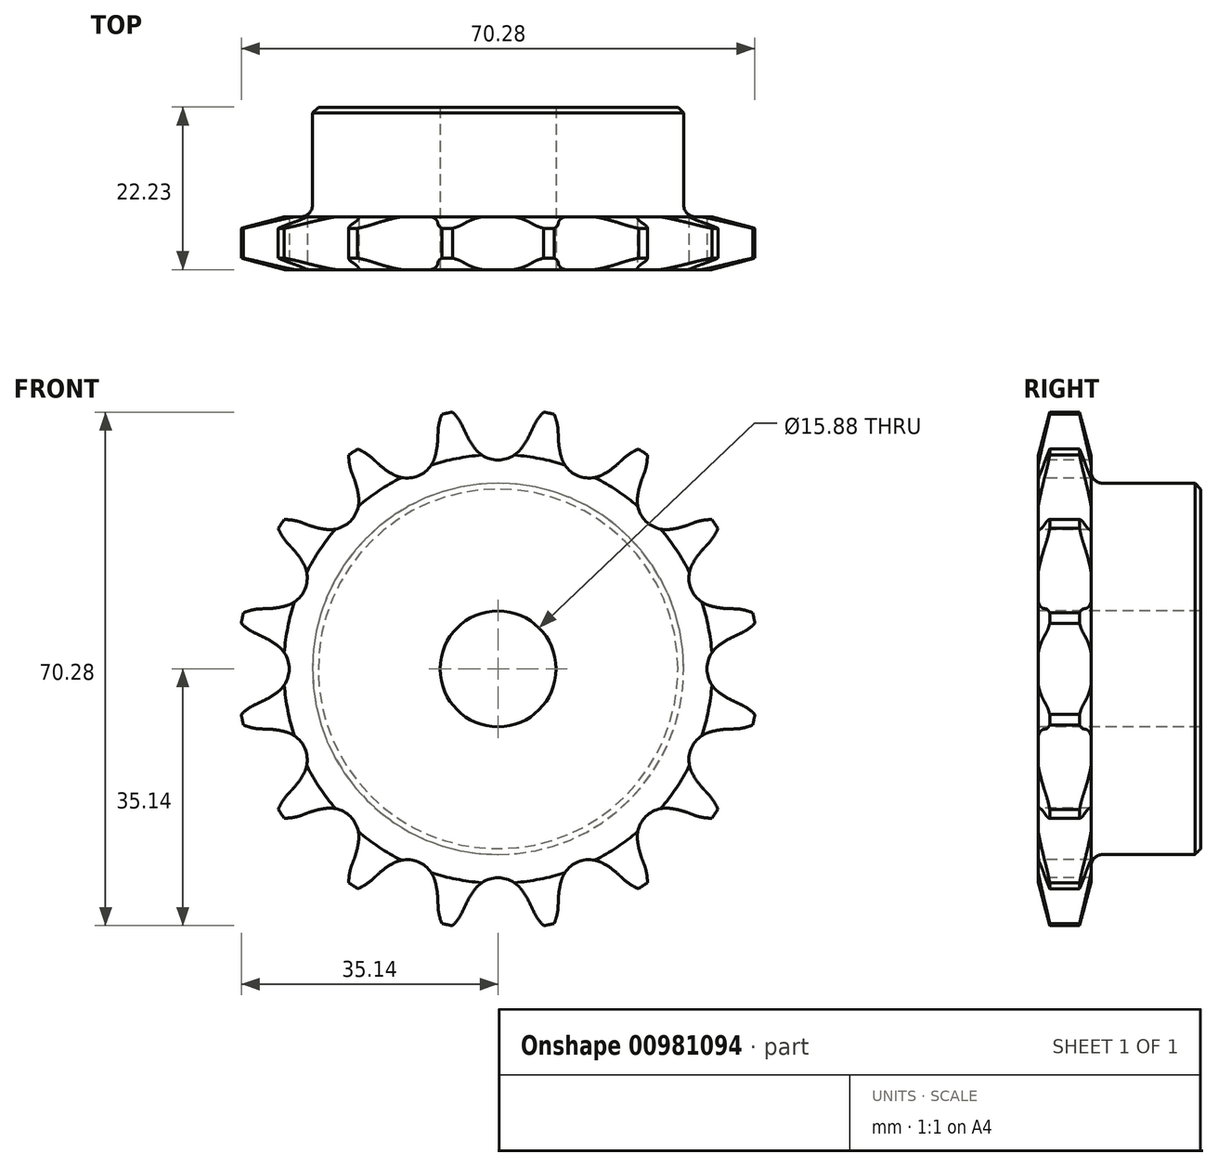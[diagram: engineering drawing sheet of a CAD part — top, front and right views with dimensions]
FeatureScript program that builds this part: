
annotation { "Feature Type Name" : "Feature", "Feature Type Description" : "" }
export const myFeature = defineFeature(function(context is Context, id is Id, definition is map)
    precondition{}
    {
        {
            var Q0;
            Q0=qCreatedBy(makeId("Right.planeOp"),FACE);
            var sketch = newSketch(context, id + "F0", { "sketchPlane" : qUnion([Q0])});
            skLineSegment(sketch, "E0", {"start": v(0, 0) * mm, "end": v(22.23, 0) * mm, "construction": true});
            skLineSegment(sketch, "E1.bottom", {"start": v(0, 35.69) * mm, "end": v(7.21, 35.69) * mm});
            skLineSegment(sketch, "E1.top", {"start": v(0, 7.94) * mm, "end": v(7.21, 7.94) * mm});
            skLineSegment(sketch, "E1.left", {"start": v(0, 35.69) * mm, "end": v(0, 7.94) * mm});
            skLineSegment(sketch, "E1.right", {"start": v(7.21, 35.69) * mm, "end": v(7.21, 7.94) * mm});
            skLineSegment(sketch, "E2.bottom", {"start": v(0, 7.94) * mm, "end": v(22.23, 7.94) * mm});
            skLineSegment(sketch, "E2.top", {"start": v(0, 25.4) * mm, "end": v(22.23, 25.4) * mm});
            skLineSegment(sketch, "E2.left", {"start": v(0, 7.94) * mm, "end": v(0, 25.4) * mm});
            skLineSegment(sketch, "E2.right", {"start": v(22.23, 7.94) * mm, "end": v(22.23, 25.4) * mm});
            skLineSegment(sketch, "E3.MirrorCS", {"start": v(0, -7.94) * mm, "end": v(7.21, -7.94) * mm});
            skLineSegment(sketch, "E4.MirrorCS", {"start": v(22.23, -7.94) * mm, "end": v(22.23, -25.4) * mm});
            skLineSegment(sketch, "E5.MirrorCS", {"start": v(0, -7.94) * mm, "end": v(22.23, -7.94) * mm});
            skLineSegment(sketch, "E6.MirrorCS", {"start": v(0, -35.69) * mm, "end": v(7.21, -35.69) * mm});
            skLineSegment(sketch, "E7.MirrorCS", {"start": v(0, -7.94) * mm, "end": v(0, -25.4) * mm});
            skLineSegment(sketch, "E8.MirrorCS", {"start": v(0, -25.4) * mm, "end": v(22.23, -25.4) * mm});
            skLineSegment(sketch, "E9.MirrorCS", {"start": v(0, -35.69) * mm, "end": v(0, -7.94) * mm});
            skLineSegment(sketch, "E10.MirrorCS", {"start": v(7.21, -35.69) * mm, "end": v(7.21, -7.94) * mm});
            skSolve(sketch);
        }
        {
            var Q0;
            {var subQ0=sQuery(id+"F0.wireOp",EDGE,"E1.bottom");Q0=makeQuery(id+"F0.imprint","IMPRINT",FACE,{"disambiguationData":[TD([[makeQuery(id+"F0.imprint","IMPRINT",EDGE,{"derivedFrom":subQ0}),-1.0]])]});}
            var Q1;
            {var subQ0=sQuery(id+"F0.wireOp",EDGE,"E1.top");Q1=makeQuery(id+"F0.imprint","IMPRINT",FACE,{"disambiguationData":[TD([[makeQuery(id+"F0.imprint","IMPRINT",EDGE,{"derivedFrom":subQ0}),1.0]])]});}
            var Q2;
            {var subQ0=sQuery(id+"F0.wireOp",EDGE,"E2.bottom");Q2=makeQuery(id+"F0.imprint","IMPRINT",FACE,{"disambiguationData":[TD([[makeQuery(id+"F0.imprint","IMPRINT",EDGE,{"derivedFrom":subQ0}),1.0]])]});}
            var Q3;
            Q3=sQuery(id+"F0.wireOp",EDGE,"E0");
            revolve(context, id + "F1", {"surfaceOperationType" : NewSurfaceOperationType.NEW, "entities" : qUnion([Q0, Q1, Q2]), "axis" : qUnion([Q3]), "revolveType" : RevolveType.FULL});
        }
        {
            var Q0;
            Q0=makeQuery(id+"F1.opRevolve","SWEPT_EDGE",EDGE,{"disambiguationData":[OSD([sQuery(id+"F0.wireOp",EDGE,"E1.right"),sQuery(id+"F0.wireOp",EDGE,"E2.top")])]});
            fillet(context, id + "F2", {"entities" : qUnion([Q0]), "radius" : 1.59 * mm, "tangentPropagation" : true, "allowEdgeOverflow" : false});
        }
        {
            var Q0;
            Q0=makeQuery(id+"F1.opRevolve","SWEPT_EDGE",EDGE,{"disambiguationData":[OSD([sQuery(id+"F0.wireOp",EDGE,"E2.top"),sQuery(id+"F0.wireOp",EDGE,"E2.right")])]});
            chamfer(context, id + "F3", {"entities" : qUnion([Q0]), "width" : 0.8 * mm, "tangentPropagation" : true});
        }
        {
            var Q0;
            Q0=makeQuery(id+"F1.opRevolve","SWEPT_EDGE",EDGE,{"disambiguationData":[OSD([sQuery(id+"F0.wireOp",EDGE,"E1.bottom"),sQuery(id+"F0.wireOp",EDGE,"E1.left")])]});
            var Q1;
            Q1=makeQuery(id+"F1.opRevolve","SWEPT_EDGE",EDGE,{"disambiguationData":[OSD([sQuery(id+"F0.wireOp",EDGE,"E1.bottom"),sQuery(id+"F0.wireOp",EDGE,"E1.right")])]});
            chamfer(context, id + "F4", {"entities" : qUnion([Q0, Q1]), "chamferType" : ChamferType.TWO_OFFSETS, "width1" : 6.35 * mm, "oppositeDirection" : false, "width2" : 1.57 * mm, "tangentPropagation" : true});
        }
        {
            var Q0;
            Q0=makeQuery(id+"F1.opRevolve","SWEPT_FACE",FACE,{"disambiguationData":[OSD([sQuery(id+"F0.wireOp",EDGE,"E1.left")])]});
            var sketch = newSketch(context, id + "F5", { "sketchPlane" : qUnion([Q0])});
            skCircle(sketch, "E11", {"center": v(0, 0) * mm, "radius": 32.55 * mm, "construction": true});
            skLineSegment(sketch, "E12", {"start": v(0, 0) * mm, "end": v(0, 32.55) * mm, "construction": true});
            skLineSegment(sketch, "E13", {"start": v(0, 32.55) * mm, "end": v(48.47, 32.55) * mm, "construction": true});
            skLineSegment(sketch, "E14", {"start": v(0, 32.55) * mm, "end": v(5, 36.56) * mm, "construction": true});
            skLineSegment(sketch, "E15", {"start": v(5, 36.56) * mm, "end": v(-4.46, 32.3) * mm, "construction": true});
            skLineSegment(sketch, "E16", {"start": v(-4.46, 32.3) * mm, "end": v(-4.82, 33.1) * mm});
            skLineSegment(sketch, "E17", {"start": v(0, 0) * mm, "end": v(-7.13, 35.85) * mm, "construction": true});
            skArc(sketch, "E18", {"start": v(-7.13, 35.85) * mm, "mid": v(-15.87, 26.15) * mm, "end": v(-4.82, 33.1) * mm, "construction": true});
            skArc(sketch, "E19", {"start": v(-4.82, 33.1) * mm, "mid": v(-5.78, 34.63) * mm, "end": v(-7.13, 35.85) * mm});
            skLineSegment(sketch, "E20", {"start": v(-4.46, 32.3) * mm, "end": v(-4.46, 32.3) * mm});
            skLineSegment(sketch, "E21", {"start": v(-4.82, 33.1) * mm, "end": v(-8.15, 40.5) * mm, "construction": true});
            skArc(sketch, "E22", {"start": v(-4.46, 32.3) * mm, "mid": v(-3.84, 31.14) * mm, "end": v(-3.1, 30.07) * mm});
            skLineSegment(sketch, "E23", {"start": v(-3.1, 30.07) * mm, "end": v(-3.1, 30.07) * mm});
            skArc(sketch, "E24.MirrorCS", {"start": v(4.46, 32.3) * mm, "mid": v(3.84, 31.14) * mm, "end": v(3.1, 30.07) * mm});
            skLineSegment(sketch, "E25.MirrorCS", {"start": v(4.46, 32.3) * mm, "end": v(4.82, 33.1) * mm});
            skArc(sketch, "E26.MirrorCS", {"start": v(4.82, 33.1) * mm, "mid": v(5.78, 34.63) * mm, "end": v(7.13, 35.85) * mm});
            skArc(sketch, "E27", {"start": v(-3.1, 30.07) * mm, "mid": v(13.83, 41.97) * mm, "end": v(-4.46, 32.3) * mm, "construction": true});
            skArc(sketch, "E28", {"start": v(3.1, 30.07) * mm, "mid": v(0, 36.51) * mm, "end": v(-3.1, 30.07) * mm, "construction": true});
            skArc(sketch, "E29", {"start": v(-3.1, 30.07) * mm, "mid": v(0, 28.59) * mm, "end": v(3.1, 30.07) * mm});
            skArc(sketch, "E30.1.0", {"start": v(-17.12, 28.74) * mm, "mid": v(-18.6, 29.79) * mm, "end": v(-20.3, 30.4) * mm});
            skLineSegment(sketch, "E30.1.1", {"start": v(-16.48, 28.14) * mm, "end": v(-17.12, 28.74) * mm});
            skArc(sketch, "E30.1.2", {"start": v(-16.48, 28.14) * mm, "mid": v(-15.47, 27.3) * mm, "end": v(-14.36, 26.6) * mm});
            skArc(sketch, "E30.1.3", {"start": v(-14.36, 26.6) * mm, "mid": v(-10.94, 26.41) * mm, "end": v(-8.65, 28.96) * mm});
            skArc(sketch, "E30.1.4", {"start": v(-8.24, 31.55) * mm, "mid": v(-8.37, 30.24) * mm, "end": v(-8.65, 28.96) * mm});
            skLineSegment(sketch, "E30.1.5", {"start": v(-8.24, 31.55) * mm, "end": v(-8.22, 32.42) * mm});
            skArc(sketch, "E30.1.6", {"start": v(-8.22, 32.42) * mm, "mid": v(-7.91, 34.21) * mm, "end": v(-7.13, 35.85) * mm});
            skArc(sketch, "E30.2.0", {"start": v(-26.8, 20) * mm, "mid": v(-28.58, 20.4) * mm, "end": v(-30.4, 20.3) * mm});
            skLineSegment(sketch, "E30.2.1", {"start": v(-26, 19.69) * mm, "end": v(-26.8, 20) * mm});
            skArc(sketch, "E30.2.2", {"start": v(-26, 19.69) * mm, "mid": v(-24.74, 19.3) * mm, "end": v(-23.45, 19.08) * mm});
            skArc(sketch, "E30.2.3", {"start": v(-23.45, 19.08) * mm, "mid": v(-20.21, 20.21) * mm, "end": v(-19.08, 23.45) * mm});
            skArc(sketch, "E30.2.4", {"start": v(-19.69, 26) * mm, "mid": v(-19.3, 24.74) * mm, "end": v(-19.08, 23.45) * mm});
            skLineSegment(sketch, "E30.2.5", {"start": v(-19.69, 26) * mm, "end": v(-20, 26.8) * mm});
            skArc(sketch, "E30.2.6", {"start": v(-20, 26.8) * mm, "mid": v(-20.4, 28.58) * mm, "end": v(-20.3, 30.4) * mm});
            skArc(sketch, "E30.3.0", {"start": v(-32.42, 8.22) * mm, "mid": v(-34.21, 7.91) * mm, "end": v(-35.85, 7.13) * mm});
            skLineSegment(sketch, "E30.3.1", {"start": v(-31.55, 8.24) * mm, "end": v(-32.42, 8.22) * mm});
            skArc(sketch, "E30.3.2", {"start": v(-31.55, 8.24) * mm, "mid": v(-30.24, 8.37) * mm, "end": v(-28.96, 8.65) * mm});
            skArc(sketch, "E30.3.3", {"start": v(-28.96, 8.65) * mm, "mid": v(-26.41, 10.94) * mm, "end": v(-26.6, 14.36) * mm});
            skArc(sketch, "E30.3.4", {"start": v(-28.14, 16.48) * mm, "mid": v(-27.3, 15.47) * mm, "end": v(-26.6, 14.36) * mm});
            skLineSegment(sketch, "E30.3.5", {"start": v(-28.14, 16.48) * mm, "end": v(-28.74, 17.12) * mm});
            skArc(sketch, "E30.3.6", {"start": v(-28.74, 17.12) * mm, "mid": v(-29.79, 18.6) * mm, "end": v(-30.4, 20.3) * mm});
            skArc(sketch, "E30.4.0", {"start": v(-33.1, -4.82) * mm, "mid": v(-34.63, -5.78) * mm, "end": v(-35.85, -7.13) * mm});
            skLineSegment(sketch, "E30.4.1", {"start": v(-32.3, -4.46) * mm, "end": v(-33.1, -4.82) * mm});
            skArc(sketch, "E30.4.2", {"start": v(-32.3, -4.46) * mm, "mid": v(-31.14, -3.84) * mm, "end": v(-30.07, -3.1) * mm});
            skArc(sketch, "E30.4.3", {"start": v(-30.07, -3.1) * mm, "mid": v(-28.59, 0) * mm, "end": v(-30.07, 3.1) * mm});
            skArc(sketch, "E30.4.4", {"start": v(-32.3, 4.46) * mm, "mid": v(-31.14, 3.84) * mm, "end": v(-30.07, 3.1) * mm});
            skLineSegment(sketch, "E30.4.5", {"start": v(-32.3, 4.46) * mm, "end": v(-33.1, 4.82) * mm});
            skArc(sketch, "E30.4.6", {"start": v(-33.1, 4.82) * mm, "mid": v(-34.63, 5.78) * mm, "end": v(-35.85, 7.13) * mm});
            skArc(sketch, "E30.5.0", {"start": v(-28.74, -17.12) * mm, "mid": v(-29.79, -18.6) * mm, "end": v(-30.4, -20.3) * mm});
            skLineSegment(sketch, "E30.5.1", {"start": v(-28.14, -16.48) * mm, "end": v(-28.74, -17.12) * mm});
            skArc(sketch, "E30.5.2", {"start": v(-28.14, -16.48) * mm, "mid": v(-27.3, -15.47) * mm, "end": v(-26.6, -14.36) * mm});
            skArc(sketch, "E30.5.3", {"start": v(-26.6, -14.36) * mm, "mid": v(-26.41, -10.94) * mm, "end": v(-28.96, -8.65) * mm});
            skArc(sketch, "E30.5.4", {"start": v(-31.55, -8.24) * mm, "mid": v(-30.24, -8.37) * mm, "end": v(-28.96, -8.65) * mm});
            skLineSegment(sketch, "E30.5.5", {"start": v(-31.55, -8.24) * mm, "end": v(-32.42, -8.22) * mm});
            skArc(sketch, "E30.5.6", {"start": v(-32.42, -8.22) * mm, "mid": v(-34.21, -7.91) * mm, "end": v(-35.85, -7.13) * mm});
            skArc(sketch, "E30.6.0", {"start": v(-20, -26.8) * mm, "mid": v(-20.4, -28.58) * mm, "end": v(-20.3, -30.4) * mm});
            skLineSegment(sketch, "E30.6.1", {"start": v(-19.69, -26) * mm, "end": v(-20, -26.8) * mm});
            skArc(sketch, "E30.6.2", {"start": v(-19.69, -26) * mm, "mid": v(-19.3, -24.74) * mm, "end": v(-19.08, -23.45) * mm});
            skArc(sketch, "E30.6.3", {"start": v(-19.08, -23.45) * mm, "mid": v(-20.21, -20.21) * mm, "end": v(-23.45, -19.08) * mm});
            skArc(sketch, "E30.6.4", {"start": v(-26, -19.69) * mm, "mid": v(-24.74, -19.3) * mm, "end": v(-23.45, -19.08) * mm});
            skLineSegment(sketch, "E30.6.5", {"start": v(-26, -19.69) * mm, "end": v(-26.8, -20) * mm});
            skArc(sketch, "E30.6.6", {"start": v(-26.8, -20) * mm, "mid": v(-28.58, -20.4) * mm, "end": v(-30.4, -20.3) * mm});
            skArc(sketch, "E30.7.0", {"start": v(-8.22, -32.42) * mm, "mid": v(-7.91, -34.21) * mm, "end": v(-7.13, -35.85) * mm});
            skLineSegment(sketch, "E30.7.1", {"start": v(-8.24, -31.55) * mm, "end": v(-8.22, -32.42) * mm});
            skArc(sketch, "E30.7.2", {"start": v(-8.24, -31.55) * mm, "mid": v(-8.37, -30.24) * mm, "end": v(-8.65, -28.96) * mm});
            skArc(sketch, "E30.7.3", {"start": v(-8.65, -28.96) * mm, "mid": v(-10.94, -26.41) * mm, "end": v(-14.36, -26.6) * mm});
            skArc(sketch, "E30.7.4", {"start": v(-16.48, -28.14) * mm, "mid": v(-15.47, -27.3) * mm, "end": v(-14.36, -26.6) * mm});
            skLineSegment(sketch, "E30.7.5", {"start": v(-16.48, -28.14) * mm, "end": v(-17.12, -28.74) * mm});
            skArc(sketch, "E30.7.6", {"start": v(-17.12, -28.74) * mm, "mid": v(-18.6, -29.79) * mm, "end": v(-20.3, -30.4) * mm});
            skArc(sketch, "E30.8.0", {"start": v(4.82, -33.1) * mm, "mid": v(5.78, -34.63) * mm, "end": v(7.13, -35.85) * mm});
            skLineSegment(sketch, "E30.8.1", {"start": v(4.46, -32.3) * mm, "end": v(4.82, -33.1) * mm});
            skArc(sketch, "E30.8.2", {"start": v(4.46, -32.3) * mm, "mid": v(3.84, -31.14) * mm, "end": v(3.1, -30.07) * mm});
            skArc(sketch, "E30.8.3", {"start": v(3.1, -30.07) * mm, "mid": v(0, -28.59) * mm, "end": v(-3.1, -30.07) * mm});
            skArc(sketch, "E30.8.4", {"start": v(-4.46, -32.3) * mm, "mid": v(-3.84, -31.14) * mm, "end": v(-3.1, -30.07) * mm});
            skLineSegment(sketch, "E30.8.5", {"start": v(-4.46, -32.3) * mm, "end": v(-4.82, -33.1) * mm});
            skArc(sketch, "E30.8.6", {"start": v(-4.82, -33.1) * mm, "mid": v(-5.78, -34.63) * mm, "end": v(-7.13, -35.85) * mm});
            skArc(sketch, "E30.9.0", {"start": v(17.12, -28.74) * mm, "mid": v(18.6, -29.79) * mm, "end": v(20.3, -30.4) * mm});
            skLineSegment(sketch, "E30.9.1", {"start": v(16.48, -28.14) * mm, "end": v(17.12, -28.74) * mm});
            skArc(sketch, "E30.9.2", {"start": v(16.48, -28.14) * mm, "mid": v(15.47, -27.3) * mm, "end": v(14.36, -26.6) * mm});
            skArc(sketch, "E30.9.3", {"start": v(14.36, -26.6) * mm, "mid": v(10.94, -26.41) * mm, "end": v(8.65, -28.96) * mm});
            skArc(sketch, "E30.9.4", {"start": v(8.24, -31.55) * mm, "mid": v(8.37, -30.24) * mm, "end": v(8.65, -28.96) * mm});
            skLineSegment(sketch, "E30.9.5", {"start": v(8.24, -31.55) * mm, "end": v(8.22, -32.42) * mm});
            skArc(sketch, "E30.9.6", {"start": v(8.22, -32.42) * mm, "mid": v(7.91, -34.21) * mm, "end": v(7.13, -35.85) * mm});
            skArc(sketch, "E30.10.0", {"start": v(26.8, -20) * mm, "mid": v(28.58, -20.4) * mm, "end": v(30.4, -20.3) * mm});
            skLineSegment(sketch, "E30.10.1", {"start": v(26, -19.69) * mm, "end": v(26.8, -20) * mm});
            skArc(sketch, "E30.10.2", {"start": v(26, -19.69) * mm, "mid": v(24.74, -19.3) * mm, "end": v(23.45, -19.08) * mm});
            skArc(sketch, "E30.10.3", {"start": v(23.45, -19.08) * mm, "mid": v(20.21, -20.21) * mm, "end": v(19.08, -23.45) * mm});
            skArc(sketch, "E30.10.4", {"start": v(19.69, -26) * mm, "mid": v(19.3, -24.74) * mm, "end": v(19.08, -23.45) * mm});
            skLineSegment(sketch, "E30.10.5", {"start": v(19.69, -26) * mm, "end": v(20, -26.8) * mm});
            skArc(sketch, "E30.10.6", {"start": v(20, -26.8) * mm, "mid": v(20.4, -28.58) * mm, "end": v(20.3, -30.4) * mm});
            skArc(sketch, "E30.11.0", {"start": v(32.42, -8.22) * mm, "mid": v(34.21, -7.91) * mm, "end": v(35.85, -7.13) * mm});
            skLineSegment(sketch, "E30.11.1", {"start": v(31.55, -8.24) * mm, "end": v(32.42, -8.22) * mm});
            skArc(sketch, "E30.11.2", {"start": v(31.55, -8.24) * mm, "mid": v(30.24, -8.37) * mm, "end": v(28.96, -8.65) * mm});
            skArc(sketch, "E30.11.3", {"start": v(28.96, -8.65) * mm, "mid": v(26.41, -10.94) * mm, "end": v(26.6, -14.36) * mm});
            skArc(sketch, "E30.11.4", {"start": v(28.14, -16.48) * mm, "mid": v(27.3, -15.47) * mm, "end": v(26.6, -14.36) * mm});
            skLineSegment(sketch, "E30.11.5", {"start": v(28.14, -16.48) * mm, "end": v(28.74, -17.12) * mm});
            skArc(sketch, "E30.11.6", {"start": v(28.74, -17.12) * mm, "mid": v(29.79, -18.6) * mm, "end": v(30.4, -20.3) * mm});
            skArc(sketch, "E30.12.0", {"start": v(33.1, 4.82) * mm, "mid": v(34.63, 5.78) * mm, "end": v(35.85, 7.13) * mm});
            skLineSegment(sketch, "E30.12.1", {"start": v(32.3, 4.46) * mm, "end": v(33.1, 4.82) * mm});
            skArc(sketch, "E30.12.2", {"start": v(32.3, 4.46) * mm, "mid": v(31.14, 3.84) * mm, "end": v(30.07, 3.1) * mm});
            skArc(sketch, "E30.12.3", {"start": v(30.07, 3.1) * mm, "mid": v(28.59, 0) * mm, "end": v(30.07, -3.1) * mm});
            skArc(sketch, "E30.12.4", {"start": v(32.3, -4.46) * mm, "mid": v(31.14, -3.84) * mm, "end": v(30.07, -3.1) * mm});
            skLineSegment(sketch, "E30.12.5", {"start": v(32.3, -4.46) * mm, "end": v(33.1, -4.82) * mm});
            skArc(sketch, "E30.12.6", {"start": v(33.1, -4.82) * mm, "mid": v(34.63, -5.78) * mm, "end": v(35.85, -7.13) * mm});
            skArc(sketch, "E30.13.0", {"start": v(28.74, 17.12) * mm, "mid": v(29.79, 18.6) * mm, "end": v(30.4, 20.3) * mm});
            skLineSegment(sketch, "E30.13.1", {"start": v(28.14, 16.48) * mm, "end": v(28.74, 17.12) * mm});
            skArc(sketch, "E30.13.2", {"start": v(28.14, 16.48) * mm, "mid": v(27.3, 15.47) * mm, "end": v(26.6, 14.36) * mm});
            skArc(sketch, "E30.13.3", {"start": v(26.6, 14.36) * mm, "mid": v(26.41, 10.94) * mm, "end": v(28.96, 8.65) * mm});
            skArc(sketch, "E30.13.4", {"start": v(31.55, 8.24) * mm, "mid": v(30.24, 8.37) * mm, "end": v(28.96, 8.65) * mm});
            skLineSegment(sketch, "E30.13.5", {"start": v(31.55, 8.24) * mm, "end": v(32.42, 8.22) * mm});
            skArc(sketch, "E30.13.6", {"start": v(32.42, 8.22) * mm, "mid": v(34.21, 7.91) * mm, "end": v(35.85, 7.13) * mm});
            skArc(sketch, "E30.14.0", {"start": v(20, 26.8) * mm, "mid": v(20.4, 28.58) * mm, "end": v(20.3, 30.4) * mm});
            skLineSegment(sketch, "E30.14.1", {"start": v(19.69, 26) * mm, "end": v(20, 26.8) * mm});
            skArc(sketch, "E30.14.2", {"start": v(19.69, 26) * mm, "mid": v(19.3, 24.74) * mm, "end": v(19.08, 23.45) * mm});
            skArc(sketch, "E30.14.3", {"start": v(19.08, 23.45) * mm, "mid": v(20.21, 20.21) * mm, "end": v(23.45, 19.08) * mm});
            skArc(sketch, "E30.14.4", {"start": v(26, 19.69) * mm, "mid": v(24.74, 19.3) * mm, "end": v(23.45, 19.08) * mm});
            skLineSegment(sketch, "E30.14.5", {"start": v(26, 19.69) * mm, "end": v(26.8, 20) * mm});
            skArc(sketch, "E30.14.6", {"start": v(26.8, 20) * mm, "mid": v(28.58, 20.4) * mm, "end": v(30.4, 20.3) * mm});
            skArc(sketch, "E30.15.0", {"start": v(8.22, 32.42) * mm, "mid": v(7.91, 34.21) * mm, "end": v(7.13, 35.85) * mm});
            skLineSegment(sketch, "E30.15.1", {"start": v(8.24, 31.55) * mm, "end": v(8.22, 32.42) * mm});
            skArc(sketch, "E30.15.2", {"start": v(8.24, 31.55) * mm, "mid": v(8.37, 30.24) * mm, "end": v(8.65, 28.96) * mm});
            skArc(sketch, "E30.15.3", {"start": v(8.65, 28.96) * mm, "mid": v(10.94, 26.41) * mm, "end": v(14.36, 26.6) * mm});
            skArc(sketch, "E30.15.4", {"start": v(16.48, 28.14) * mm, "mid": v(15.47, 27.3) * mm, "end": v(14.36, 26.6) * mm});
            skLineSegment(sketch, "E30.15.5", {"start": v(16.48, 28.14) * mm, "end": v(17.12, 28.74) * mm});
            skArc(sketch, "E30.15.6", {"start": v(17.12, 28.74) * mm, "mid": v(18.6, 29.79) * mm, "end": v(20.3, 30.4) * mm});
            skSolve(sketch);
        }
        {
            var Q0;
            Q0 = qSketchRegion(id + "F5", true);
            extrude(context, id + "F6", {"entities" : qUnion([Q0]), "operationType" : NewBodyOperationType.INTERSECT, "endBound" : BoundingType.THROUGH_ALL, "oppositeDirection" : true, "depth" : 25.4 * mm, "offsetDistance" : 25.4 * mm});
        }
    });
